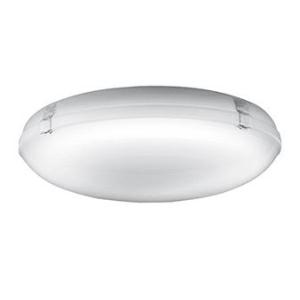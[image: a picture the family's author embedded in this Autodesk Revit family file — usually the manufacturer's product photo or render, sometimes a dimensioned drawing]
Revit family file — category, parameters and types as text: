
# Revit family: 3f_filippi_-_3f_petra_3f_filippi_-_34332_-_3f_petra_op_380_22w_led_ep
name_source: partatom
category: Lighting Fixtures
units: mm (PartAtom-declared; Revit-internal decimal feet)

## family parameters
Cut with Voids When Loaded = No
Host = Face
Light Source = No
Part Type = Normal
Room Calculation Point = No
Round Connector Dimension = Use Diameter
Shared = No

## types (1)
- 3F Filippi - 3F Petra (1 x LED, 2978 lm, 26 W, 4000 K)
    Apparent Load = 26 VA
    Approval mark = ENEC
    CIE Flux Codes = 43 73 91 90 100
    Color Rendering = 80
    Color Temperature = 4000 K
    Control Gear = Electronic ballast
    Default Elevation = 1800 mm
    Description = ILLUMINOTECHNICAL
Luminous efficiency 100% (DLOR 90%, ULOR 10%).
Initial luminous flux of the luminaire 2978 lm.
Emergency luminaire luminous flux BLF 15.7%.
Diffused symmetric distribution.
Installation Interdistance Transv.D = 1.26 x hu - Long.D = 1.25 x hu.
Tabular UGR (CIE 117 - 4H-8H; S=0.25H; 70/50/20): RUG 21.3 - 21.2.
Beam angle: 117° - 116°.
Luminous efficacy 115 lm/W.
Lifetime (L93/B10): 30000 h. (tq+25°C)
Lifetime (L90/B10): 50000 h. (tq+25°C)
Lifetime (L85/B10): 80000 h. (tq+25°C)
Lifetime (L80/B10): 100000 h. (tq+25°C)
Sudden decreased luminous flux after 50000 hours: 0% (C0).
Photobiological safety in compliance with IEC/TR 62778: RG0 risk exempt, (IEC 62471).
In compliance with IEC/EN 62722-2-1 - IEC/EN 62717 standards.

SOURCE
Circular LED module 22W/840.
Energy efficiency class (UE 2019/2020 - UE 2019/2015): C.
CIE 13.3 Colour rendering index: CRI >80 (R9 <50%).
IES TM-30 Fidelity Index: Rf = 84 Rg = 95.
CCT nominal colour temperature 4000 K.
Colour initial tolerance (MacAdam): SDCM 3.

MECHANICAL
Housing in glazed self-extinguishing V2 polycarbonate, UV stabilised, injection moulded.
Ecologic anti-aging injected sealing gasket.
Gear-tray reflector unit in aluminium, painted in white polyester, fixed to the housing by quick-fastening steel devices, hinged opening.
Diffuser in opal methacrylate (PMMA), injection moulded.
Snug fit safety snap-lock clips for diffuser mounting in transparent polycarbonate, screwdriver opening.
Luminaire with limited surface temperature. - D - (EN 60598-2-24)
Dimensions: diameter 380 mm, height 117 mm. Weight 2 kg.
IP64 protection degree.
Mechanical strength to impacts IK02 (0.2 joule).
Glow-wire test resistance 650°C.

ELECTRICAL
Halogen Free electronic wiring 230V-50/60Hz, power factor 0.90, THD <25%, constant output current, SELV, class I, 1 driver.
Power of the luminaire 26 W.
CE - IEC 60598-1 - EN 60598-1.
EP maintained emergency wiring on board, 1h duration, 24h recharge; compliant with EN 60598-2-22, excluding high risk areas.
SAFE FLICKER: PstLM=<1 and SVM=<0.4 (IEC TR 61547-1 and IEC TR 63158), to ensure a more comfortable and safe light.
Ambient temperature from +5°C to +25°C.
Temperature class T6 max 85°C.
Relative humidity UR: <85%.

INSTALLATION
Ceiling / Wall.

APPLICATIONS
Suitable product for food production plants (HACCP), IFS (Food Version 6), BRC (GSFS Food Version 7).
Transit areas, stairwells. Environments where a diffused lighting provides visual comfort.
Virtually in all environments compatibly with the emissions/atmospheres compromising the use of plastic materials. Not suitable for installation on surfaces subject to important vibrations, exposed to weather conditions.

WARNING
Luminaire designed for disposal/recycling at end-of-life.
Replaceable (LED only) light source by a professional. Replaceable control gear by a professional.
    Height = 117 mm
    Lamp = 1 x LED
    Lamp Light Flux = 2978 lm
    Lamp Power = 26 W
    Lamp count = 1
    Length = 380 mm
    Lifetime = 50000 h
    Luminous efficacy = 115 lm/W
    Manufacturer = 3F Filippi
    ModVariant = No
    Model = 3F Filippi - 34332 - 3F Petra OP 380 22W LED EP
    Mounting Place = Ceiling
    Mounting Type = Surface mounted
    Number of Poles = 1
    OnlyDefault = Yes
    Power Factor = 1
    Product Name = 3F Filippi - 3F Petra
    Product group = ceiling mounted luminaire
    ProductGroupID = 3
    Protection Class = Protection class I
    Protection Degree = IP 64
    RLX_Detail_Level = 1
    RLX_Emergency_Light_Flux = 0 lm
    RLX_Emergency_Type = 0
    RLX_Emergency_Type_DB = No
    RlxData = <blob elided: 219769 chars, md5=8fe313eb>
    Socket = socket
    Standby Power = 0 W
    System Light Flux = 2978 lm
    System Power = 26 W
    Type Comments = Product without accessories
    Type Image = 3ffilippi_34332.jpg
    URL = http://relux.com
    VarID = ---
    Voltage = 0 V
    Weight = 0.00 kg
    Width = 0 mm  [stored 0 ft]

note: [stored X ft] marks values corroborated as IEEE doubles in the binary element streams (Revit-internal decimal feet)

## geometry (parser evidence)
native form markers: Blend x4, Sweep x11
no freeform markers — native parametric forms only
